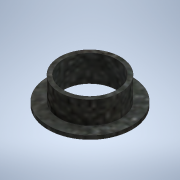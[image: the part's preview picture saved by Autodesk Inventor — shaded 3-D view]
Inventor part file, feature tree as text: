
AUTODESK INVENTOR PART (.ipt)
format: ipt  version: 2020.2 (Build 242310000, 310)  size: 118,272 bytes
history: native  units: mm
features: extrude x2, other x1, sketch x1
ambient origin geometry x8: Origin, YZ Plane, XZ Plane, XY Plane, X Axis, Y Axis, Z Axis, Center Point
bodies: Body1 (feature_tree)
feature tree (4):
  other  "ソリッド1"
  sketch  "スケッチ1"
  extrude  "押し出し1"  Depth=14.0mm
  extrude  "押し出し2"  Depth=16.0mm
